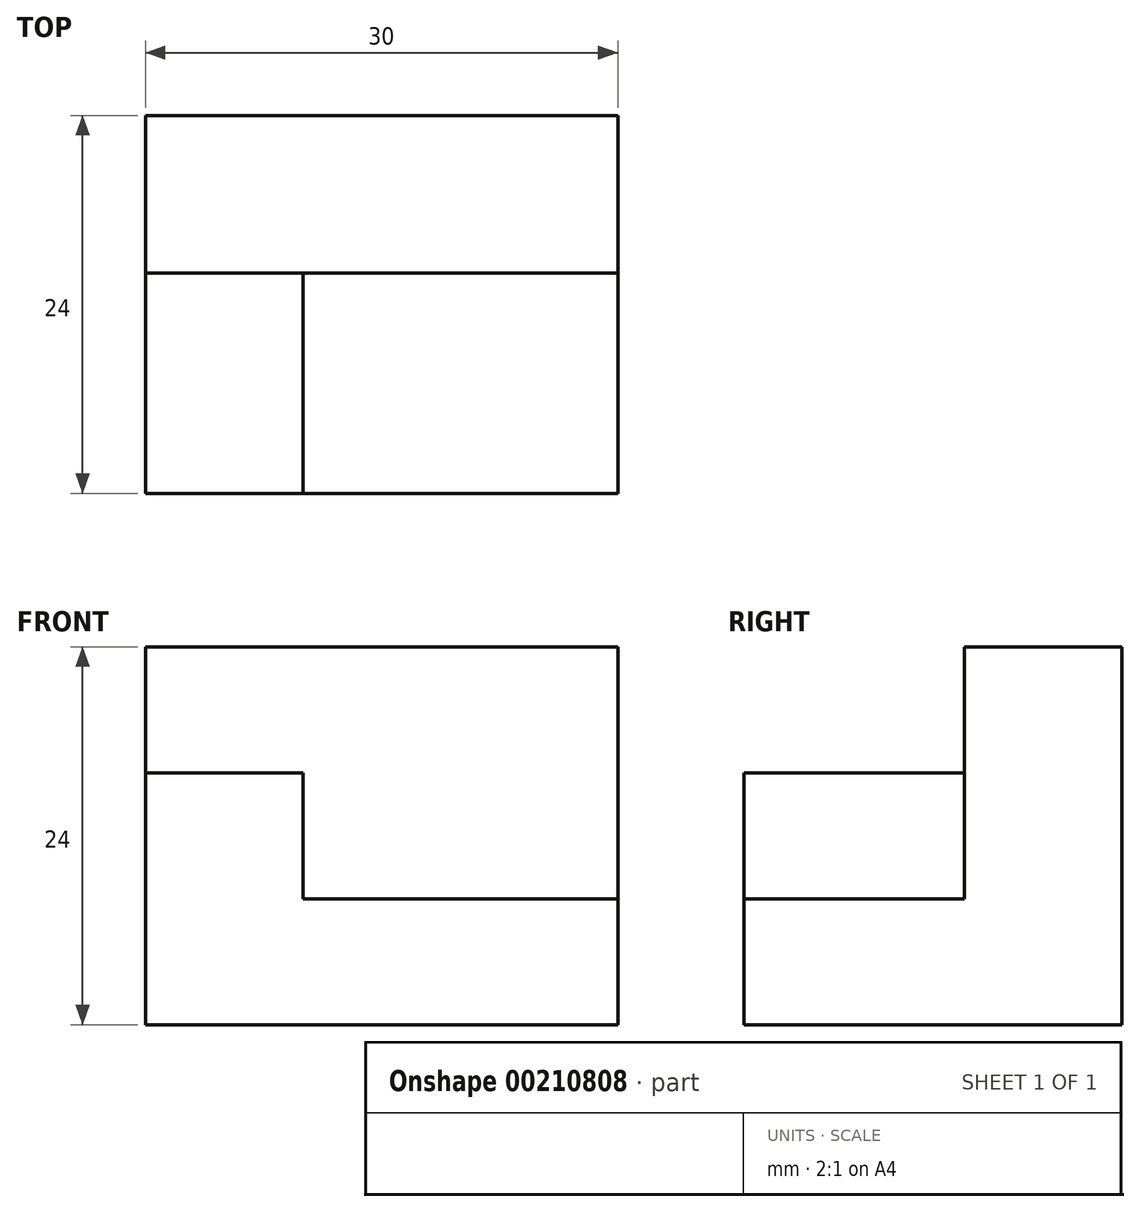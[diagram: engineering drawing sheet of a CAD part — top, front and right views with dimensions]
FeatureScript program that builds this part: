
annotation { "Feature Type Name" : "Feature", "Feature Type Description" : "" }
export const myFeature = defineFeature(function(context is Context, id is Id, definition is map)
    precondition{}
    {
        {
            var Q0;
            Q0=qCreatedBy(makeId("Top.planeOp"),FACE);
            var sketch = newSketch(context, id + "F0", { "sketchPlane" : qUnion([Q0])});
            skLineSegment(sketch, "E0.bottom", {"start": v(0, 0) * mm, "end": v(30, 0) * mm});
            skLineSegment(sketch, "E0.top", {"start": v(0, 24) * mm, "end": v(30, 24) * mm});
            skLineSegment(sketch, "E0.left", {"start": v(0, 0) * mm, "end": v(0, 24) * mm});
            skLineSegment(sketch, "E0.right", {"start": v(30, 0) * mm, "end": v(30, 24) * mm});
            skSolve(sketch);
        }
        {
            var Q0;
            Q0=makeQuery(id+"F0.imprint","IMPRINT",FACE,{"disambiguationData":[TD([[makeQuery(id+"F0.imprint","IMPRINT",EDGE,{"derivedFrom":sQuery(id+"F0.wireOp",EDGE,"E0.bottom")}),1.0]])]});
            extrude(context, id + "F1", {"entities" : qUnion([Q0]), "depth" : 24 * mm});
        }
        {
            var Q0;
            Q0=makeQuery(id+"F1.opExtrude","SWEPT_FACE",FACE,{"disambiguationData":[OSD([sQuery(id+"F0.wireOp",EDGE,"E0.right")])]});
            var sketch = newSketch(context, id + "F2", { "sketchPlane" : qUnion([Q0])});
            skPoint(sketch, "E1.orphan", {"position": v(8.15, 7.52) * mm});
            skPoint(sketch, "E2.end.orphan", {"position": v(8.15, 6.36) * mm});
            skLineSegment(sketch, "E3", {"start": v(24, 24) * mm, "end": v(24, 0) * mm});
            skLineSegment(sketch, "E4", {"start": v(24, 0) * mm, "end": v(0, 0) * mm});
            skLineSegment(sketch, "E5", {"start": v(0, 0) * mm, "end": v(0, 8) * mm});
            skLineSegment(sketch, "E6", {"start": v(0, 8) * mm, "end": v(14, 8) * mm});
            skLineSegment(sketch, "E7", {"start": v(14, 8) * mm, "end": v(14, 24) * mm});
            skLineSegment(sketch, "E8", {"start": v(14, 24) * mm, "end": v(24, 24) * mm});
            skSolve(sketch);
        }
        {
            var Q0;
            {var subQ0=sQuery(id+"F2.wireOp",EDGE,"E6");Q0=makeQuery(id+"F2.imprint","IMPRINT",FACE,{"disambiguationData":[TD([[makeQuery(id+"F2.imprint","IMPRINT",EDGE,{"derivedFrom":subQ0}),1.0]])]});}
            extrude(context, id + "F3", {"entities" : qUnion([Q0]), "operationType" : NewBodyOperationType.REMOVE, "oppositeDirection" : true, "depth" : 20 * mm});
        }
        {
            var Q0;
            Q0=makeQuery(id+"F1.opExtrude","SWEPT_FACE",FACE,{"disambiguationData":[OSD([sQuery(id+"F0.wireOp",EDGE,"E0.bottom")])]});
            var sketch = newSketch(context, id + "F4", { "sketchPlane" : qUnion([Q0])});
            skLineSegment(sketch, "E9.bottom", {"start": v(0, 24) * mm, "end": v(10, 24) * mm});
            skLineSegment(sketch, "E9.top", {"start": v(0, 8) * mm, "end": v(10, 8) * mm});
            skLineSegment(sketch, "E9.left", {"start": v(0, 24) * mm, "end": v(0, 8) * mm});
            skLineSegment(sketch, "E9.right", {"start": v(10, 24) * mm, "end": v(10, 8) * mm});
            skLineSegment(sketch, "E10", {"start": v(0, 16) * mm, "end": v(10, 16) * mm});
            skSolve(sketch);
        }
        {
            var Q0;
            {var subQ0=sQuery(id+"F4.wireOp",EDGE,"E9.bottom");Q0=makeQuery(id+"F4.imprint","IMPRINT",FACE,{"disambiguationData":[TD([[makeQuery(id+"F4.imprint","IMPRINT",EDGE,{"derivedFrom":subQ0}),-1.0]])]});}
            extrude(context, id + "F5", {"entities" : qUnion([Q0]), "operationType" : NewBodyOperationType.REMOVE, "oppositeDirection" : true, "depth" : 14 * mm});
        }
    });
